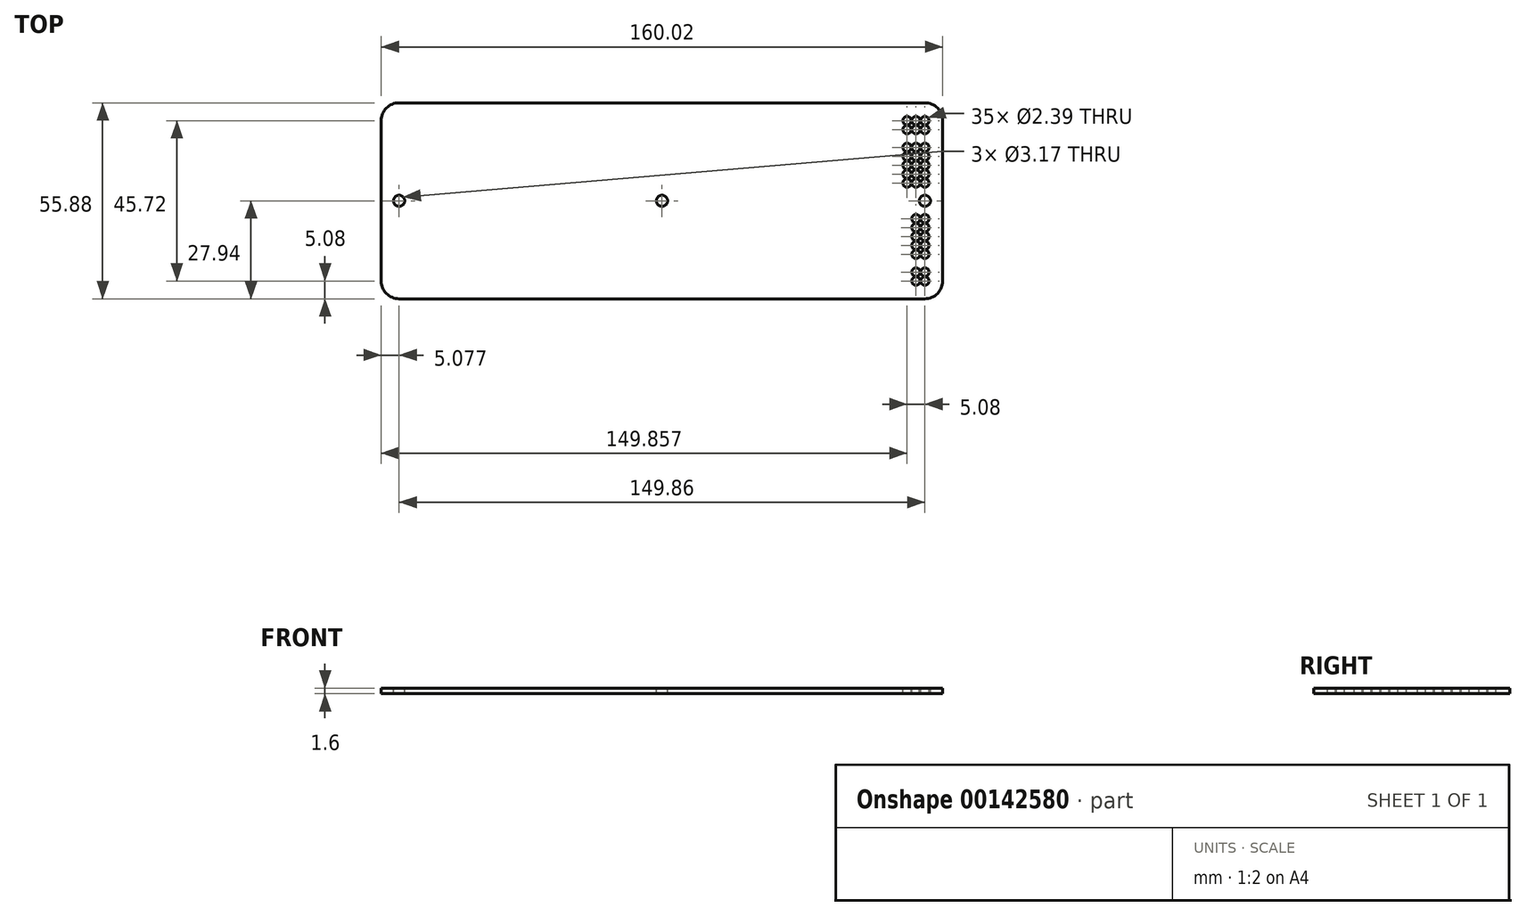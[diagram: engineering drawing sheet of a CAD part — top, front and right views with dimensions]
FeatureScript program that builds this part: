
annotation { "Feature Type Name" : "Feature", "Feature Type Description" : "" }
export const myFeature = defineFeature(function(context is Context, id is Id, definition is map)
    precondition{}
    {
        {
            var Q0;
            Q0=qCreatedBy(makeId("Top.planeOp"),FACE);
            var sketch = newSketch(context, id + "F0", { "sketchPlane" : qUnion([Q0])});
            skLineSegment(sketch, "E0", {"start": v(-94.25, 5.08) * mm, "end": v(-19.32, 5.08) * mm});
            skLineSegment(sketch, "E1", {"start": v(-19.32, 5.08) * mm, "end": v(55.6, 5.08) * mm});
            skLineSegment(sketch, "E2", {"start": v(55.6, -10.16) * mm, "end": v(55.6, -7.62) * mm});
            skLineSegment(sketch, "E3", {"start": v(55.6, -7.62) * mm, "end": v(55.6, -5.08) * mm});
            skLineSegment(sketch, "E4", {"start": v(55.6, -5.08) * mm, "end": v(55.6, -2.54) * mm});
            skLineSegment(sketch, "E5", {"start": v(55.6, -2.54) * mm, "end": v(55.6, 0) * mm});
            skLineSegment(sketch, "E6", {"start": v(55.6, -10.16) * mm, "end": v(55.6, -15.24) * mm});
            skLineSegment(sketch, "E7", {"start": v(55.6, -15.24) * mm, "end": v(55.6, -17.78) * mm});
            skLineSegment(sketch, "E8", {"start": v(55.6, 5.08) * mm, "end": v(55.6, 0) * mm});
            skPoint(sketch, "E9", {"position": v(55.6, 5.08) * mm});
            skPoint(sketch, "E10", {"position": v(55.6, 0) * mm});
            skPoint(sketch, "E11", {"position": v(55.6, -2.54) * mm});
            skPoint(sketch, "E12", {"position": v(55.6, -5.08) * mm});
            skPoint(sketch, "E13", {"position": v(55.6, -7.62) * mm});
            skPoint(sketch, "E14", {"position": v(55.6, -10.16) * mm});
            skPoint(sketch, "E15", {"position": v(55.6, -15.24) * mm});
            skPoint(sketch, "E16", {"position": v(55.6, -17.78) * mm});
            skLineSegment(sketch, "E17.MirrorCS", {"start": v(55.6, 5.08) * mm, "end": v(55.6, 10.16) * mm});
            skPoint(sketch, "E18.MirrorP", {"position": v(55.6, 10.16) * mm});
            skLineSegment(sketch, "E19.MirrorCS", {"start": v(55.6, 12.7) * mm, "end": v(55.6, 10.16) * mm});
            skPoint(sketch, "E20.MirrorP", {"position": v(55.6, 12.7) * mm});
            skLineSegment(sketch, "E21.MirrorCS", {"start": v(55.6, 15.24) * mm, "end": v(55.6, 12.7) * mm});
            skPoint(sketch, "E22.MirrorP", {"position": v(55.6, 15.24) * mm});
            skLineSegment(sketch, "E23.MirrorCS", {"start": v(55.6, 17.78) * mm, "end": v(55.6, 15.24) * mm});
            skPoint(sketch, "E24.MirrorP", {"position": v(55.6, 17.78) * mm});
            skLineSegment(sketch, "E25.MirrorCS", {"start": v(55.6, 20.32) * mm, "end": v(55.6, 17.78) * mm});
            skPoint(sketch, "E26.MirrorP", {"position": v(55.6, 20.32) * mm});
            skLineSegment(sketch, "E27.MirrorCS", {"start": v(55.6, 20.32) * mm, "end": v(55.6, 25.4) * mm});
            skPoint(sketch, "E28.MirrorP", {"position": v(55.6, 25.4) * mm});
            skLineSegment(sketch, "E29.MirrorCS", {"start": v(55.6, 25.4) * mm, "end": v(55.6, 27.94) * mm});
            skPoint(sketch, "E30.MirrorP", {"position": v(55.6, 27.94) * mm});
            skLineSegment(sketch, "E31", {"start": v(55.6, -17.78) * mm, "end": v(55.6, -22.86) * mm});
            skLineSegment(sketch, "E32", {"start": v(55.6, -22.86) * mm, "end": v(60.69, -22.86) * mm});
            skLineSegment(sketch, "E33", {"start": v(55.6, -22.86) * mm, "end": v(-94.25, -22.86) * mm});
            skLineSegment(sketch, "E34", {"start": v(-94.25, -22.86) * mm, "end": v(-99.33, -22.86) * mm});
            skLineSegment(sketch, "E35.MirrorCS", {"start": v(-94.25, 33.02) * mm, "end": v(-99.33, 33.02) * mm});
            skLineSegment(sketch, "E36.MirrorCS", {"start": v(55.6, 33.02) * mm, "end": v(-94.25, 33.02) * mm});
            skLineSegment(sketch, "E37.MirrorCS", {"start": v(55.6, 33.02) * mm, "end": v(60.69, 33.02) * mm});
            skLineSegment(sketch, "E38", {"start": v(60.69, -22.86) * mm, "end": v(60.69, 33.02) * mm});
            skLineSegment(sketch, "E39", {"start": v(-99.33, 33.02) * mm, "end": v(-99.33, -22.86) * mm});
            skCircle(sketch, "E40", {"center": v(55.6, 27.94) * mm, "radius": 1.2 * mm});
            skCircle(sketch, "E41", {"center": v(55.6, 25.4) * mm, "radius": 1.2 * mm});
            skCircle(sketch, "E42", {"center": v(55.6, 20.32) * mm, "radius": 1.2 * mm});
            skCircle(sketch, "E43", {"center": v(55.6, 17.78) * mm, "radius": 1.2 * mm});
            skCircle(sketch, "E44", {"center": v(55.6, 15.24) * mm, "radius": 1.2 * mm});
            skCircle(sketch, "E45", {"center": v(55.6, 12.7) * mm, "radius": 1.2 * mm});
            skCircle(sketch, "E46", {"center": v(55.6, 10.16) * mm, "radius": 1.2 * mm});
            skCircle(sketch, "E47", {"center": v(55.6, 0) * mm, "radius": 1.2 * mm});
            skCircle(sketch, "E48", {"center": v(55.6, -2.54) * mm, "radius": 1.2 * mm});
            skCircle(sketch, "E49", {"center": v(55.6, -5.08) * mm, "radius": 1.2 * mm});
            skCircle(sketch, "E50", {"center": v(55.6, -7.62) * mm, "radius": 1.2 * mm});
            skCircle(sketch, "E51", {"center": v(55.6, -10.16) * mm, "radius": 1.2 * mm});
            skCircle(sketch, "E52", {"center": v(55.6, -15.24) * mm, "radius": 1.2 * mm});
            skCircle(sketch, "E53", {"center": v(55.6, -17.78) * mm, "radius": 1.2 * mm});
            skCircle(sketch, "E54.1.0.0", {"center": v(53.07, 27.94) * mm, "radius": 1.2 * mm});
            skCircle(sketch, "E54.1.0.1", {"center": v(53.07, 25.4) * mm, "radius": 1.2 * mm});
            skCircle(sketch, "E54.1.0.2", {"center": v(53.07, 20.32) * mm, "radius": 1.2 * mm});
            skCircle(sketch, "E54.1.0.3", {"center": v(53.07, 17.78) * mm, "radius": 1.2 * mm});
            skCircle(sketch, "E54.1.0.4", {"center": v(53.07, 15.24) * mm, "radius": 1.2 * mm});
            skCircle(sketch, "E54.1.0.5", {"center": v(53.07, 12.7) * mm, "radius": 1.2 * mm});
            skCircle(sketch, "E54.1.0.6", {"center": v(53.07, 10.16) * mm, "radius": 1.2 * mm});
            skCircle(sketch, "E54.1.0.7", {"center": v(53.07, 0) * mm, "radius": 1.2 * mm});
            skCircle(sketch, "E54.1.0.8", {"center": v(53.07, -2.54) * mm, "radius": 1.2 * mm});
            skCircle(sketch, "E54.1.0.9", {"center": v(53.07, -5.08) * mm, "radius": 1.2 * mm});
            skCircle(sketch, "E54.1.0.10", {"center": v(53.07, -7.62) * mm, "radius": 1.2 * mm});
            skCircle(sketch, "E54.1.0.11", {"center": v(53.07, -10.16) * mm, "radius": 1.2 * mm});
            skCircle(sketch, "E54.1.0.12", {"center": v(53.07, -15.24) * mm, "radius": 1.2 * mm});
            skCircle(sketch, "E54.1.0.13", {"center": v(53.07, -17.78) * mm, "radius": 1.2 * mm});
            skCircle(sketch, "E54.2.0.0", {"center": v(50.53, 27.94) * mm, "radius": 1.2 * mm});
            skCircle(sketch, "E54.2.0.1", {"center": v(50.53, 25.4) * mm, "radius": 1.2 * mm});
            skCircle(sketch, "E54.2.0.2", {"center": v(50.53, 20.32) * mm, "radius": 1.2 * mm});
            skCircle(sketch, "E54.2.0.3", {"center": v(50.53, 17.78) * mm, "radius": 1.2 * mm});
            skCircle(sketch, "E54.2.0.4", {"center": v(50.53, 15.24) * mm, "radius": 1.2 * mm});
            skCircle(sketch, "E54.2.0.5", {"center": v(50.53, 12.7) * mm, "radius": 1.2 * mm});
            skCircle(sketch, "E54.2.0.6", {"center": v(50.53, 10.16) * mm, "radius": 1.2 * mm});
            skLineSegment(sketch, "E54.direction1", {"start": v(55.6, 27.94) * mm, "end": v(53.07, 27.94) * mm, "construction": true});
            skSolve(sketch);
        }
        {
            var Q0;
            Q0=makeQuery(id+"F0.imprint","IMPRINT",FACE,{"disambiguationData":[TD([[makeQuery(id+"F0.imprint","IMPRINT",EDGE,{"derivedFrom":sQuery(id+"F0.wireOp",EDGE,"E32")}),1.0]])]});
            extrude(context, id + "F1", {"entities" : qUnion([Q0]), "oppositeDirection" : true, "depth" : 1.6 * mm});
        }
        {
            var Q0;
            Q0=sQuery(id+"F0.wireOp",VERTEX,"E0.start");
            var Q1;
            Q1=sQuery(id+"F0.wireOp",VERTEX,"E1.start");
            var Q2;
            Q2=sQuery(id+"F0.wireOp",VERTEX,"E9");
            var Q3;
            Q3=makeQuery(id+"F1.opExtrude","SWEPT_BODY",BODY,{"disambiguationData":[OSD([sQuery(id+"F0.wireOp",EDGE,"E32"),sQuery(id+"F0.wireOp",EDGE,"E33"),sQuery(id+"F0.wireOp",EDGE,"E34"),sQuery(id+"F0.wireOp",EDGE,"E35.MirrorCS"),sQuery(id+"F0.wireOp",EDGE,"E36.MirrorCS"),sQuery(id+"F0.wireOp",EDGE,"E37.MirrorCS"),sQuery(id+"F0.wireOp",EDGE,"E38"),sQuery(id+"F0.wireOp",EDGE,"E39")])]});
            hole(context, id + "F2", {"style" : HoleStyle.SIMPLE, "endStyle" : HoleEndStyle.THROUGH, "holeDiameter" : 3.17 * mm, "locations" : qUnion([Q0, Q1, Q2]), "scope" : qUnion([Q3]), "isTappedThrough" : true});
        }
        {
            var Q0;
            Q0=makeQuery(id+"F1.opExtrude","SWEPT_EDGE",EDGE,{"disambiguationData":[OSD([sQuery(id+"F0.wireOp",EDGE,"E32"),sQuery(id+"F0.wireOp",EDGE,"E38")])]});
            var Q1;
            Q1=makeQuery(id+"F1.opExtrude","SWEPT_EDGE",EDGE,{"disambiguationData":[OSD([sQuery(id+"F0.wireOp",EDGE,"E37.MirrorCS"),sQuery(id+"F0.wireOp",EDGE,"E38")])]});
            var Q2;
            Q2=makeQuery(id+"F1.opExtrude","SWEPT_EDGE",EDGE,{"disambiguationData":[OSD([sQuery(id+"F0.wireOp",EDGE,"E34"),sQuery(id+"F0.wireOp",EDGE,"E39")])]});
            var Q3;
            Q3=makeQuery(id+"F1.opExtrude","SWEPT_EDGE",EDGE,{"disambiguationData":[OSD([sQuery(id+"F0.wireOp",EDGE,"E35.MirrorCS"),sQuery(id+"F0.wireOp",EDGE,"E39")])]});
            fillet(context, id + "F3", {"entities" : qUnion([Q0, Q1, Q2, Q3]), "radius" : 5.08 * mm, "tangentPropagation" : true, "allowEdgeOverflow" : false});
        }
    });
